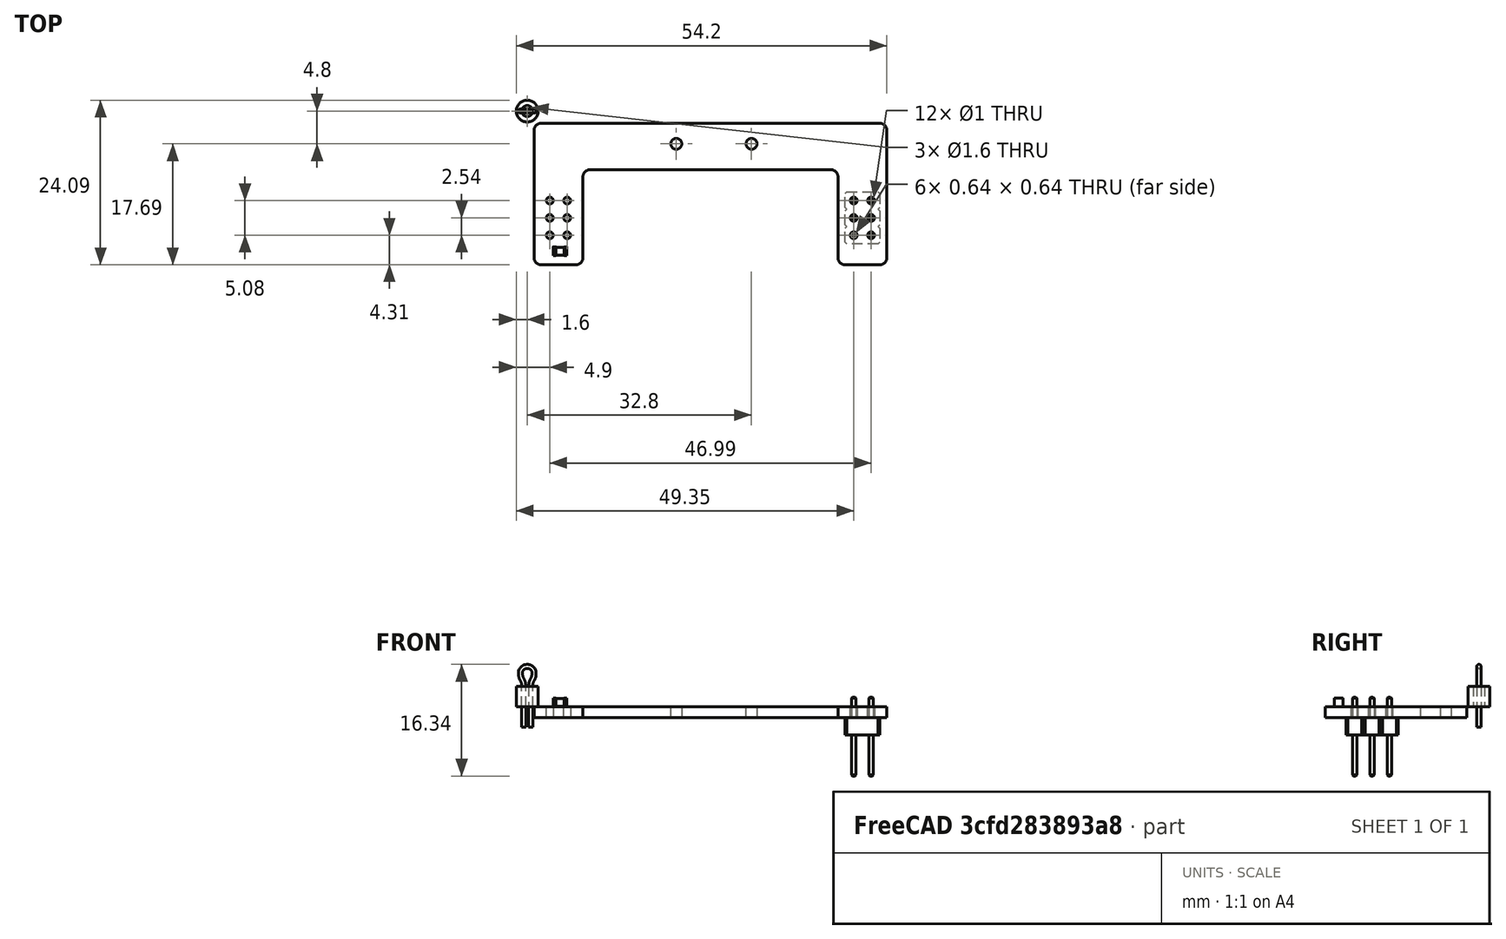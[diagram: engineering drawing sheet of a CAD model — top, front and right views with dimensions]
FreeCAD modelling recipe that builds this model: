
FCSTD DOCUMENT  (FreeCAD 1.0R39109 (Git))
Label: breadboard_pwr_jumper
License: All rights reserved
LicenseURL: http://en.wikipedia.org/wiki/All_rights_reserved
objects: App::Part×6, Part::Feature×5, App::Link×3, PartDesign::CoordinateSystem×1, Sketcher::SketchObject×1
note: 8 computed .brp shape members not serialized (recipe doc carries the construction recipe); baked Part::Feature solids carry a one-line shape summary decoded from their .brp

FEATURE [PartDesign::CoordinateSystem] Local_CS_7d9
  AttacherType = Attacher::AttachEngine3D
  MapMode = 2
FEATURE [Part::Feature] Pcb_7d9
  Placement = pos=(-96.7,86.9,0) rot=(0,0,1;0rad)
  shape: bbox 51.6 x 20.69 x 1.6 mm, 32 faces (baked)
FEATURE [Sketcher::SketchObject] PCB_Sketch_7d9
  ArcFitTolerance = 1e-06
  FullyConstrained = false
  MakeInternals = false
  sketch-geometry (16):
    g0: LineSegment StartX=9.15 StartY=-8.6 StartZ=0 EndX=44.45 EndY=-8.6 EndZ=0
    g1: LineSegment StartX=2 StartY=-22.49 StartZ=0 EndX=7.15 EndY=-22.49 EndZ=0
    g2: LineSegment StartX=2 StartY=-1.8 StartZ=0 EndX=51.6 EndY=-1.8 EndZ=0
    g3: LineSegment StartX=8.15 StartY=-21.49 StartZ=0 EndX=8.15 EndY=-9.6 EndZ=0
    g4: LineSegment StartX=1 StartY=-21.49 StartZ=0 EndX=1 EndY=-2.8 EndZ=0
    g5: LineSegment StartX=45.45 StartY=-21.49 StartZ=0 EndX=45.45 EndY=-9.6 EndZ=0
    g6: LineSegment StartX=51.6 StartY=-22.49 StartZ=0 EndX=46.45 EndY=-22.49 EndZ=0
    g7: LineSegment StartX=52.6 StartY=-21.49 StartZ=0 EndX=52.6 EndY=-2.8 EndZ=0
    g8: ArcOfCircle CenterX=51.6 CenterY=-2.8 CenterZ=0 NormalX=0 NormalY=0 NormalZ=-1 AngleXU=1.5708 Radius=0.999999 StartAngle=0 EndAngle=1.5708
    g9: ArcOfCircle CenterX=44.45 CenterY=-9.6 CenterZ=0 NormalX=0 NormalY=0 NormalZ=-1 AngleXU=1.5708 Radius=0.999999 StartAngle=0 EndAngle=1.5708
    g10: ArcOfCircle CenterX=51.6 CenterY=-21.49 CenterZ=0 NormalX=0 NormalY=0 NormalZ=-1 AngleXU=3.14159 Radius=0.999999 StartAngle=0 EndAngle=1.5708
    g11: ArcOfCircle CenterX=7.15 CenterY=-21.49 CenterZ=0 NormalX=0 NormalY=0 NormalZ=-1 AngleXU=3.14159 Radius=0.999999 StartAngle=0 EndAngle=1.5708
    g12: ArcOfCircle CenterX=46.45 CenterY=-21.49 CenterZ=0 NormalX=0 NormalY=0 NormalZ=-1 AngleXU=-1.5708 Radius=0.999999 StartAngle=0 EndAngle=1.5708
    g13: ArcOfCircle CenterX=2 CenterY=-2.8 CenterZ=0 NormalX=0 NormalY=0 NormalZ=-1 AngleXU=-7.47076e-07 Radius=0.999999 StartAngle=0 EndAngle=1.5708
    g14: ArcOfCircle CenterX=2 CenterY=-21.49 CenterZ=0 NormalX=0 NormalY=0 NormalZ=-1 AngleXU=-1.5708 Radius=0.999999 StartAngle=0 EndAngle=1.5708
    g15: ArcOfCircle CenterX=9.15 CenterY=-9.6 CenterZ=0 NormalX=0 NormalY=0 NormalZ=-1 AngleXU=-7.47076e-07 Radius=0.999999 StartAngle=0 EndAngle=1.5708
  constraints (16):
    c: Coincident(g4,g14)
    c: Coincident(g4,g13)
    c: Coincident(g1,g14)
    c: Coincident(g2,g13)
    c: Coincident(g1,g11)
    c: Coincident(g3,g11)
    c: Coincident(g3,g15)
    c: Coincident(g0,g15)
    c: Coincident(g0,g9)
    c: Coincident(g5,g12)
    c: Coincident(g5,g9)
    c: Coincident(g6,g12)
    c: Coincident(g6,g10)
    c: Coincident(g2,g8)
    c: Coincident(g7,g10)
    c: Coincident(g7,g8)
FEATURE [App::Part] Board_Geoms_7d9
  Group = -> [Pcb_7d9,PCB_Sketch_7d9]
  Origin = -> Origin
FEATURE [Part::Feature] Part__Feature  label="TestPoint_Loop_D2_60mm_Drill1_6mm_Beaded_cp"
  shape: bbox 3.2 x 3.2 x 3 mm, 4 faces (baked)
FEATURE [Part::Feature] Part__Feature001  label="TestPoint_Loop_D2_60mm_Drill1_6mm_Beaded_cp001"
  shape: bbox 3.649 x 1.14 x 9.307 mm, 7 faces (baked)
FEATURE [App::Part] TestPoint_Loop_D2_60mm_Drill1_6mm_Beaded_cp  label="TP2_TestPoint_Loop_D2_60mm_Drill1_6mm_Beaded_cp002_7cb059528ccf"
  Group = -> [Part__Feature,Part__Feature001]
  Origin = -> Origin008
  Placement = pos=(21.8,-4.8,0) rot=(0,0,1;1.5708rad)
FEATURE [Part::Feature] Shape  label="C1_C_0805_2012Metric_d11e3281cf23"
  Placement = pos=(4.8,-20.51,0) rot=(0,0,1;3.14159rad)
  shape: bbox 2 x 1.25 x 1.25 mm, 28 faces (baked)
FEATURE [App::Link] C1_C_0805_2012Metric_d11e3281cf23_ln_  label="C2_C_0805_2012Metric_a89b75c6775d"
  LinkPlacement = pos=(49.25,-20.51,0) rot=(0,0,1;3.14159rad)
  LinkedObject = -> Shape
  Placement = pos=(49.25,-20.51,0) rot=(0,0,1;3.14159rad)
FEATURE [App::Link] TP2_TestPoint_Loop_D2_60mm_Drill1_6mm_Beaded_cp002_7cb059528ccf_ln_  label="TP1_TestPoint_Loop_D2_60mm_Drill1_6mm_Beaded_cp002_d089108b461f"
  LinkPlacement = pos=(32.8,-4.8,0) rot=(0,0,1;1.5708rad)
  LinkedObject = -> TestPoint_Loop_D2_60mm_Drill1_6mm_Beaded_cp
  Placement = pos=(32.8,-4.8,0) rot=(0,0,1;1.5708rad)
FEATURE [App::Part] Top_7d9
  Group = -> [TestPoint_Loop_D2_60mm_Drill1_6mm_Beaded_cp,Shape,C1_C_0805_2012Metric_d11e3281cf23_ln_,TP2_TestPoint_Loop_D2_60mm_Drill1_6mm_Beaded_cp002_7cb059528ccf_ln_]
  Origin = -> Origin003
FEATURE [Part::Feature] Shape001  label="J2_PinHeader_2x03_P254mm_Vertical_d06323dcb5aa"
  Placement = pos=(50.29,-13.1,-1.6) rot=(0,1,0;3.14159rad)
  shape: bbox 5.08 x 7.62 x 11.54 mm, 130 faces (baked)
FEATURE [App::Link] J2_PinHeader_2x03_P254mm_Vertical_d06323dcb5aa_ln_  label="J1_PinHeader_2x03_P254mm_Vertical_cb8854c45253"
  LinkPlacement = pos=(5.84,-13.1,-1.6) rot=(0,1,0;3.14159rad)
  LinkedObject = -> Shape001
  Placement = pos=(5.84,-13.1,-1.6) rot=(0,1,0;3.14159rad)
FEATURE [App::Part] Bot_7d9
  Group = -> [Shape001,J2_PinHeader_2x03_P254mm_Vertical_d06323dcb5aa_ln_]
  Origin = -> Origin004
FEATURE [App::Part] Step_Models_7d9
  Group = -> [Top_7d9,Bot_7d9]
  Origin = -> Origin002
FEATURE [App::Part] Board_7d9  label="breadboard_pwr_jumper"
  Group = -> [Local_CS_7d9,Board_Geoms_7d9,Step_Models_7d9]
  Origin = -> Origin001
